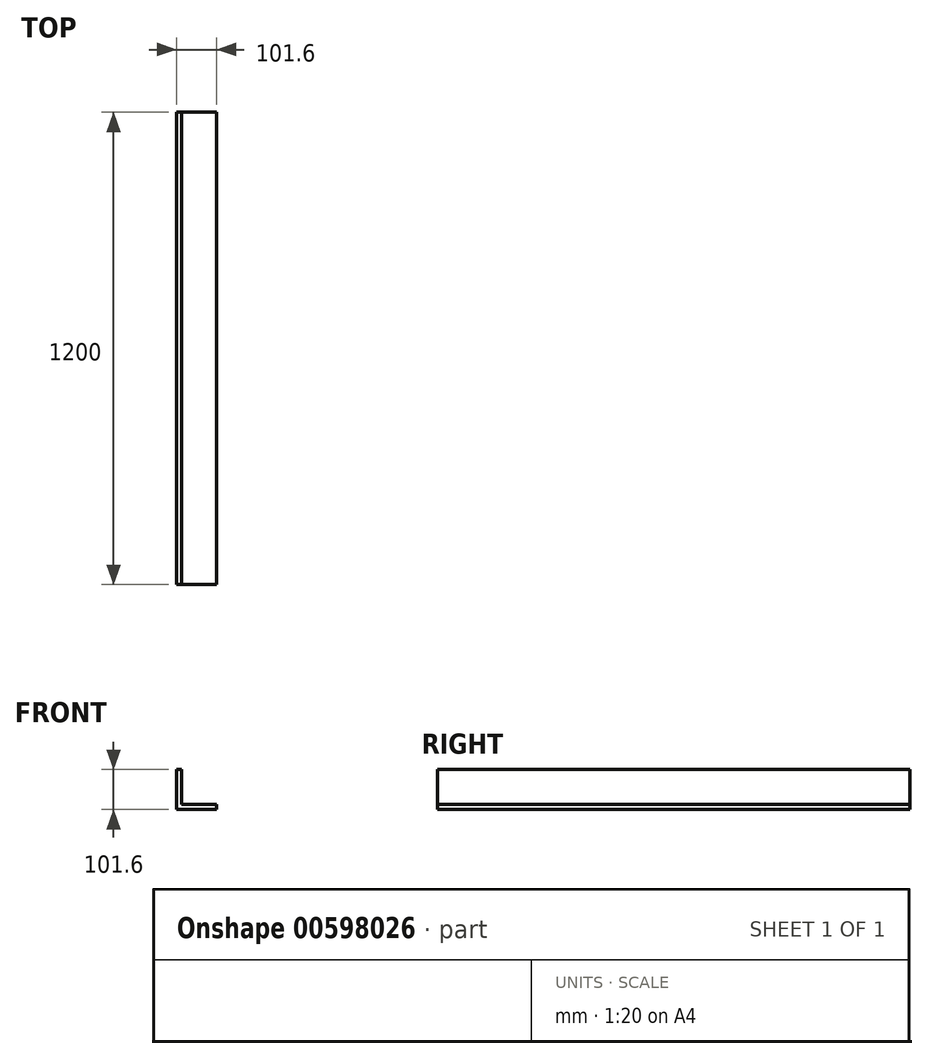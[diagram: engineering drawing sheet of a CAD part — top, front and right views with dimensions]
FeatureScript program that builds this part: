
annotation { "Feature Type Name" : "Feature", "Feature Type Description" : "" }
export const myFeature = defineFeature(function(context is Context, id is Id, definition is map)
    precondition{}
    {
        {
            var Q0;
            Q0=qCreatedBy(makeId("Front.planeOp"),FACE);
            var sketch = newSketch(context, id + "F0", { "sketchPlane" : qUnion([Q0])});
            skLineSegment(sketch, "E0.bottom", {"start": v(-81.55, 70.13) * mm, "end": v(-68.85, 70.13) * mm});
            skLineSegment(sketch, "E0.top", {"start": v(-81.55, -18.77) * mm, "end": v(-68.85, -18.77) * mm});
            skLineSegment(sketch, "E0.left", {"start": v(-81.55, 70.13) * mm, "end": v(-81.55, -18.77) * mm});
            skLineSegment(sketch, "E0.right", {"start": v(-68.85, 70.13) * mm, "end": v(-68.85, -18.77) * mm});
            skLineSegment(sketch, "E1.bottom", {"start": v(-81.55, -18.77) * mm, "end": v(20.05, -18.77) * mm});
            skLineSegment(sketch, "E1.top", {"start": v(-81.55, -31.47) * mm, "end": v(20.05, -31.47) * mm});
            skLineSegment(sketch, "E1.left", {"start": v(-81.55, -18.77) * mm, "end": v(-81.55, -31.47) * mm});
            skLineSegment(sketch, "E1.right", {"start": v(20.05, -18.77) * mm, "end": v(20.05, -31.47) * mm});
            skSolve(sketch);
        }
        {
            var Q0;
            Q0 = qSketchRegion(id + "F0", true);
            extrude(context, id + "F1", {"entities" : qUnion([Q0]), "depth" : 1200 * mm, "offsetDistance" : 25.4 * mm});
        }
    });
